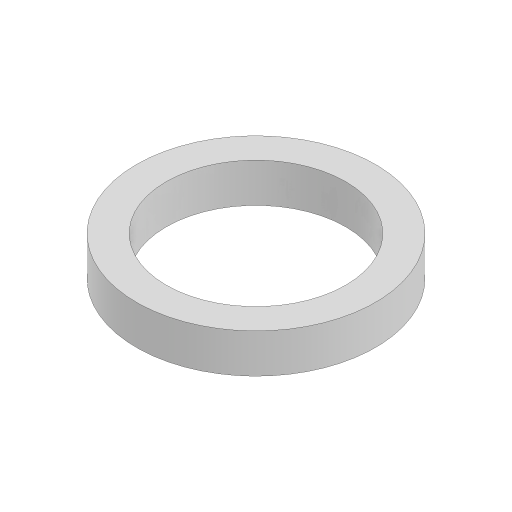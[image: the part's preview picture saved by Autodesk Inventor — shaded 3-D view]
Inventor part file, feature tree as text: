
AUTODESK INVENTOR PART (.ipt)
format: ipt  version: 2024 (Build 280153000, 153)  size: 98,304 bytes
history: native  units: in
note: dims shown in document units (in); Inventor stores cm internally (conversion verified against a paired STEP export)
features: extrude x1, direct_edit x1, sketch x1, other x1
ambient origin geometry x8: Origin, YZ Plane, XZ Plane, XY Plane, X Axis, Y Axis, Z Axis, Center Point
bodies: Solid1 (feature_tree)
feature tree (4):
  extrude  "Extrusion1"  Depth=0.25in
  direct_edit  "Direct Edit1"
  sketch  "Sketch1"  dims[d0=1.125in d1=0.2in d2=0.25in d3=0.0in d4=-0.01in]
  other  "Size1"
